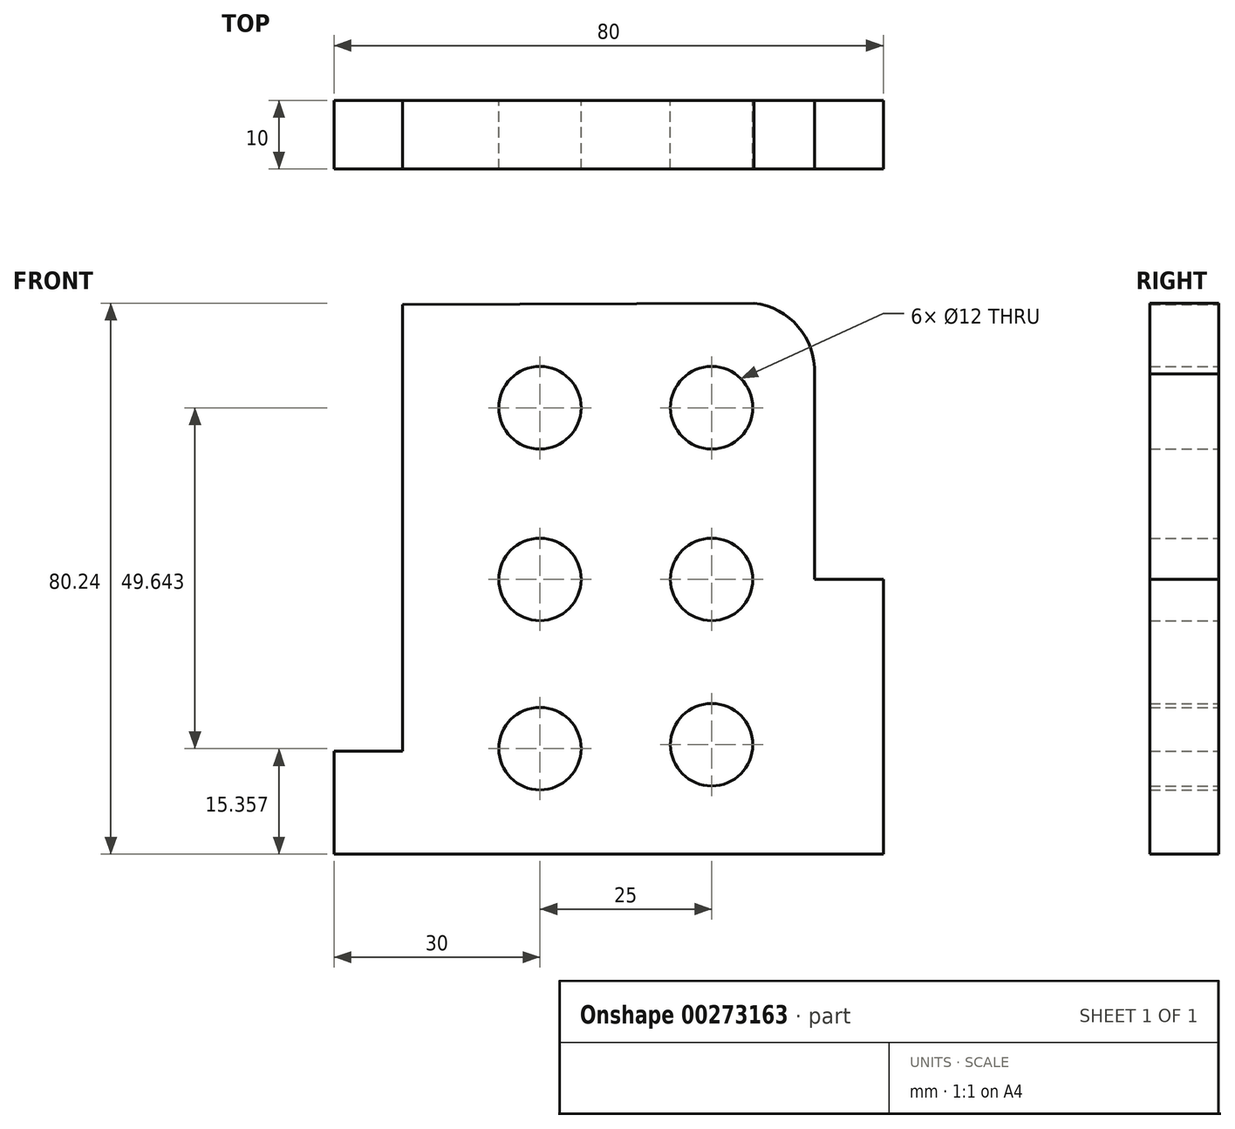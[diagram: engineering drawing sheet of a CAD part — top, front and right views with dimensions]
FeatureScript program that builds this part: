
annotation { "Feature Type Name" : "Feature", "Feature Type Description" : "" }
export const myFeature = defineFeature(function(context is Context, id is Id, definition is map)
    precondition{}
    {
        {
            var Q0;
            Q0=qCreatedBy(makeId("Front.planeOp"),FACE);
            var sketch = newSketch(context, id + "F0", { "sketchPlane" : qUnion([Q0])});
            skLineSegment(sketch, "E0", {"start": v(0, 0) * mm, "end": v(80, 0) * mm});
            skLineSegment(sketch, "E1", {"start": v(0, 0) * mm, "end": v(0, 15) * mm});
            skLineSegment(sketch, "E2", {"start": v(0, 15) * mm, "end": v(10, 15) * mm});
            skLineSegment(sketch, "E3", {"start": v(10, 15) * mm, "end": v(10, 80) * mm});
            skLineSegment(sketch, "E4", {"start": v(80, 0) * mm, "end": v(80, 40) * mm});
            skLineSegment(sketch, "E5", {"start": v(80, 40) * mm, "end": v(70, 40) * mm});
            skLineSegment(sketch, "E6", {"start": v(70, 40) * mm, "end": v(70, 69.93) * mm});
            skLineSegment(sketch, "E7", {"start": v(10, 80) * mm, "end": v(61.2, 80.24) * mm});
            skArc(sketch, "E8", {"start": v(70, 69.93) * mm, "mid": v(67.61, 76.8) * mm, "end": v(61.2, 80.24) * mm});
            skCircle(sketch, "E9", {"center": v(30, 15.36) * mm, "radius": 6 * mm});
            skCircle(sketch, "E10", {"center": v(55, 15.93) * mm, "radius": 6 * mm});
            skCircle(sketch, "E11", {"center": v(30, 40) * mm, "radius": 6 * mm});
            skCircle(sketch, "E12", {"center": v(30, 65) * mm, "radius": 6 * mm});
            skCircle(sketch, "E13", {"center": v(55, 40) * mm, "radius": 6 * mm});
            skCircle(sketch, "E14", {"center": v(55, 65) * mm, "radius": 6 * mm});
            skSolve(sketch);
        }
        {
            var Q0;
            Q0 = qSketchRegion(id + "F0", true);
            extrude(context, id + "F1", {"entities" : qUnion([Q0]), "depth" : 10 * mm});
        }
    });
